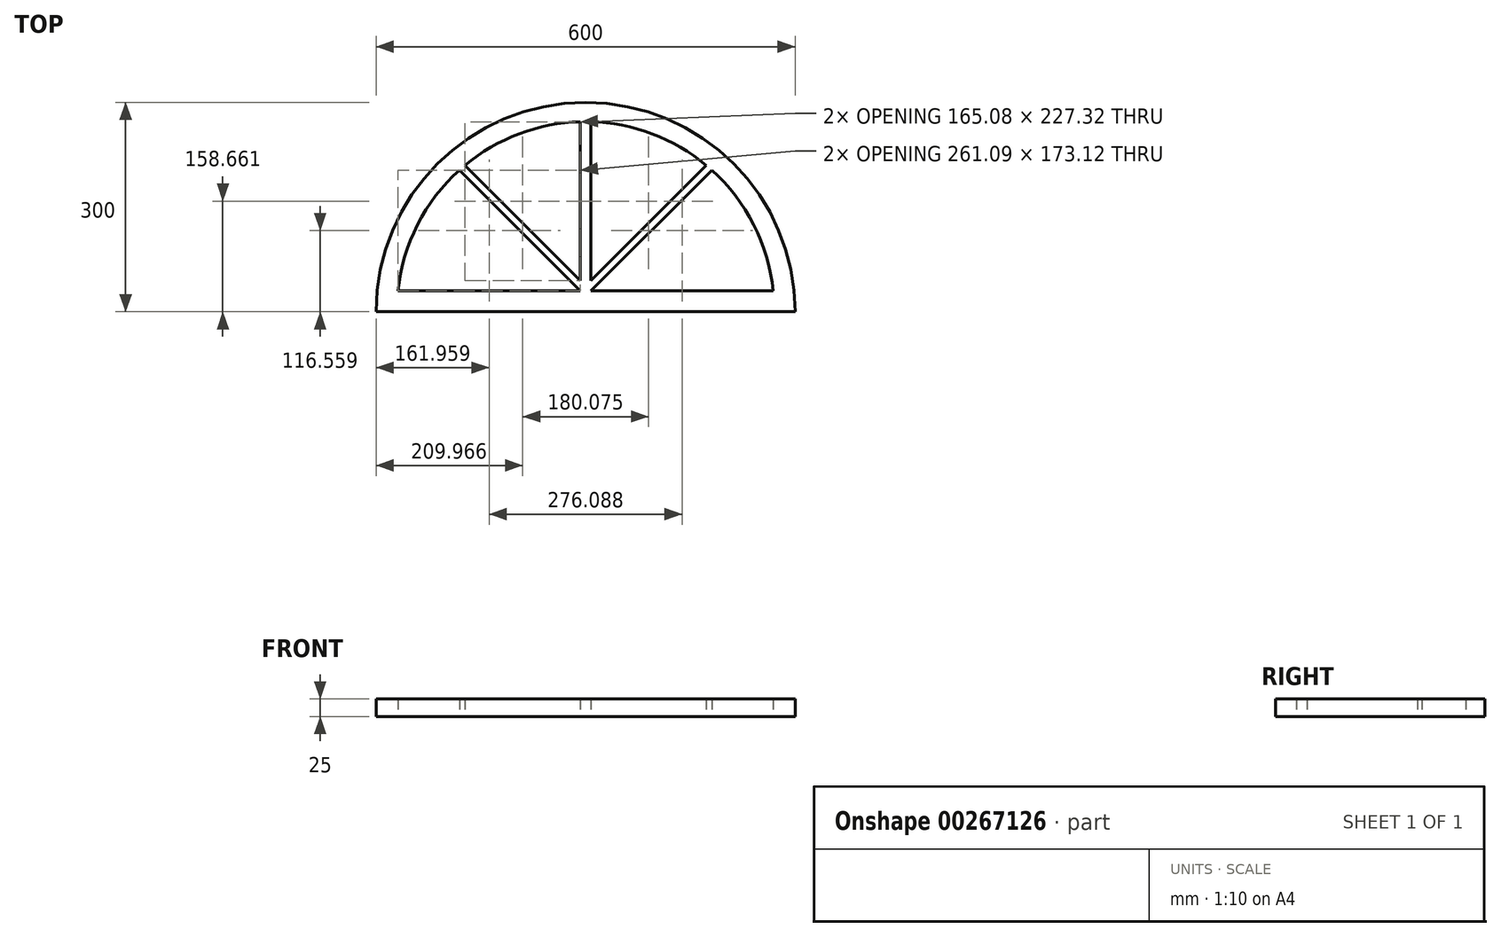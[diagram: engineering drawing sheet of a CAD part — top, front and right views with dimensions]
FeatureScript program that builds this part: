
annotation { "Feature Type Name" : "Feature", "Feature Type Description" : "" }
export const myFeature = defineFeature(function(context is Context, id is Id, definition is map)
    precondition{}
    {
        {
            var Q0;
            Q0=qCreatedBy(makeId("Top.planeOp"),FACE);
            var sketch = newSketch(context, id + "F0", { "sketchPlane" : qUnion([Q0])});
            skLineSegment(sketch, "E0", {"start": v(-65.75, -30) * mm, "end": v(534.25, -30) * mm});
            skArc(sketch, "E1", {"start": v(534.25, -30) * mm, "mid": v(234.25, 270) * mm, "end": v(-65.75, -30) * mm});
            skArc(sketch, "E2", {"start": v(502.84, 0) * mm, "mid": v(474.96, 94.74) * mm, "end": v(414.87, 173.12) * mm});
            skLineSegment(sketch, "E3", {"start": v(-34.34, 0) * mm, "end": v(226.75, 0) * mm});
            skLineSegment(sketch, "E4", {"start": v(241.75, 0) * mm, "end": v(414.87, 173.12) * mm});
            skLineSegment(sketch, "E5", {"start": v(226.75, 0) * mm, "end": v(53.64, 173.12) * mm});
            skPoint(sketch, "E6.start.orphan", {"position": v(234.25, 0) * mm});
            skLineSegment(sketch, "E7", {"start": v(241.75, 15) * mm, "end": v(241.75, 242.32) * mm});
            skLineSegment(sketch, "E8", {"start": v(241.75, 15) * mm, "end": v(406.83, 180.08) * mm});
            skLineSegment(sketch, "E9", {"start": v(226.75, 15) * mm, "end": v(61.68, 180.08) * mm});
            skLineSegment(sketch, "E10", {"start": v(226.75, 15) * mm, "end": v(226.75, 242.32) * mm});
            skLineSegment(sketch, "E11.trimOffspring", {"start": v(241.75, 0) * mm, "end": v(502.84, 0) * mm});
            skArc(sketch, "E12.trimOffspring", {"start": v(226.75, 242.32) * mm, "mid": v(138.99, 225.06) * mm, "end": v(61.68, 180.08) * mm});
            skArc(sketch, "E13.trimOffspring", {"start": v(53.64, 173.12) * mm, "mid": v(-6.45, 94.74) * mm, "end": v(-34.34, 0) * mm});
            skArc(sketch, "E14.trimOffspring", {"start": v(406.83, 180.08) * mm, "mid": v(329.52, 225.06) * mm, "end": v(241.75, 242.32) * mm});
            skSolve(sketch);
        }
        {
            var Q0;
            Q0 = qSketchRegion(id + "F0", true);
            extrude(context, id + "F1", {"entities" : qUnion([Q0]), "depth" : 25 * mm});
        }
    });
